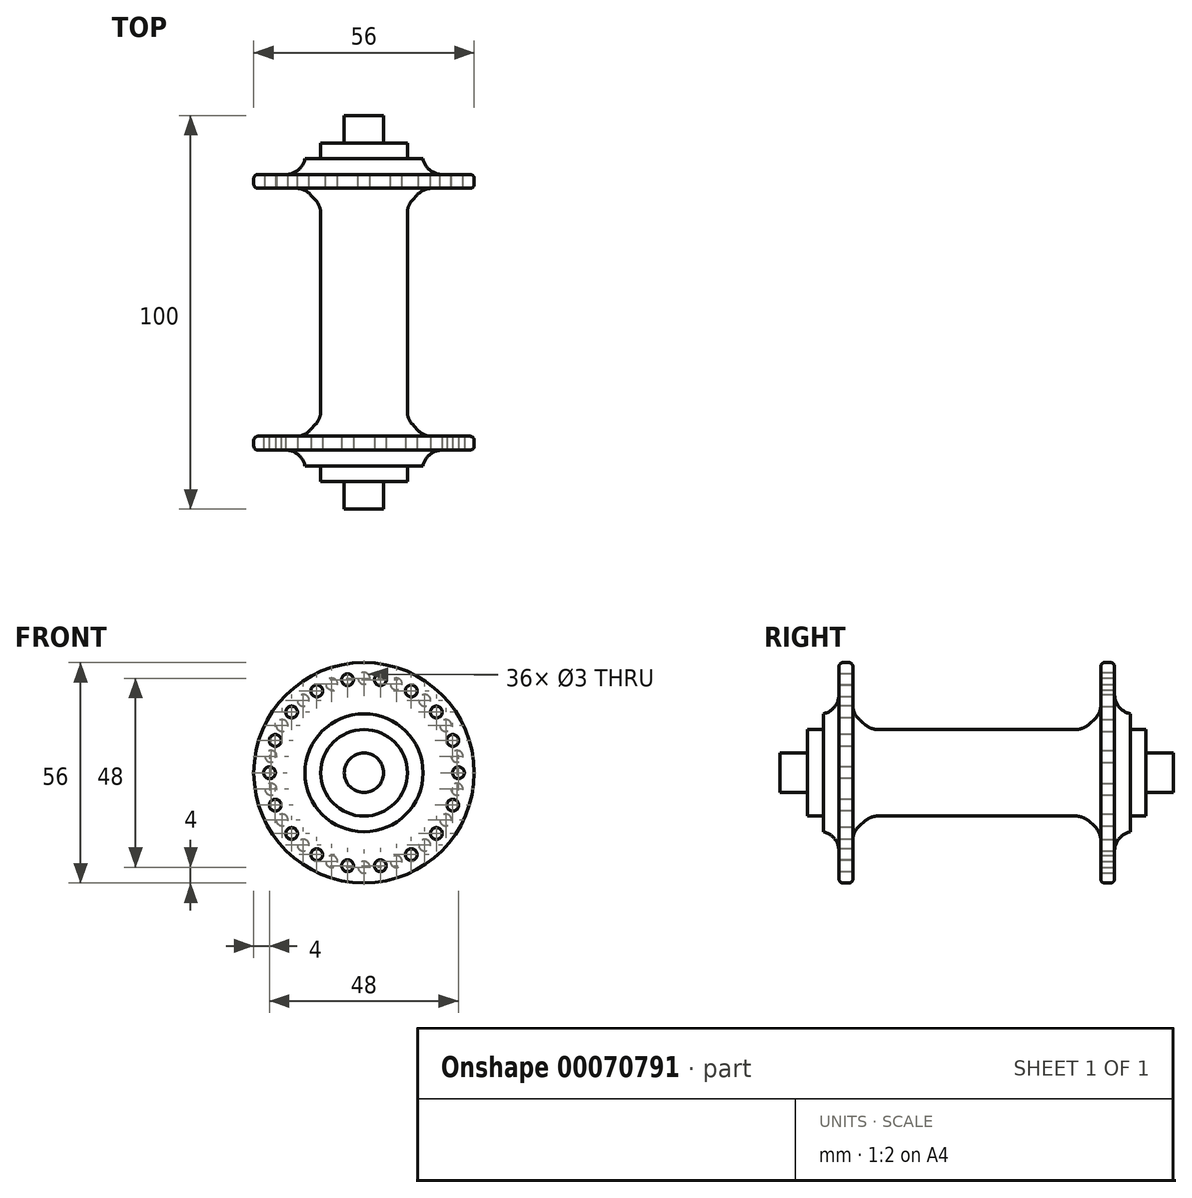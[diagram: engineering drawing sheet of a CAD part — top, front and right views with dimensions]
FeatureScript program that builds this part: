
annotation { "Feature Type Name" : "Feature", "Feature Type Description" : "" }
export const myFeature = defineFeature(function(context is Context, id is Id, definition is map)
    precondition{}
    {
        {
            var Q0;
            Q0=qCreatedBy(makeId("Top.planeOp"),FACE);
            var sketch = newSketch(context, id + "F0", { "sketchPlane" : qUnion([Q0])});
            skLineSegment(sketch, "E0", {"start": v(0, 0) * mm, "end": v(0, 50) * mm});
            skLineSegment(sketch, "E1", {"start": v(0, 50) * mm, "end": v(5, 50) * mm});
            skLineSegment(sketch, "E2", {"start": v(5, 50) * mm, "end": v(5, 43) * mm});
            skLineSegment(sketch, "E3", {"start": v(5, 43) * mm, "end": v(11, 43) * mm});
            skLineSegment(sketch, "E4", {"start": v(11, 43) * mm, "end": v(11, 39) * mm});
            skLineSegment(sketch, "E5", {"start": v(11, 39) * mm, "end": v(15, 39) * mm});
            skLineSegment(sketch, "E6", {"start": v(15, 39) * mm, "end": v(15, 35) * mm});
            skLineSegment(sketch, "E7", {"start": v(15, 35) * mm, "end": v(28, 35) * mm});
            skLineSegment(sketch, "E8", {"start": v(28, 35) * mm, "end": v(28, 31.5) * mm});
            skLineSegment(sketch, "E9", {"start": v(28, 31.5) * mm, "end": v(15, 31.5) * mm});
            skLineSegment(sketch, "E10", {"start": v(15, 31.5) * mm, "end": v(11, 27.03) * mm});
            skLineSegment(sketch, "E11", {"start": v(11, 27.03) * mm, "end": v(11, 0) * mm});
            skLineSegment(sketch, "E12", {"start": v(11, 0) * mm, "end": v(0, 0) * mm});
            skSolve(sketch);
        }
        {
            var Q0;
            Q0=makeQuery(id+"F0.imprint","IMPRINT",FACE,{"disambiguationData":[TD([[makeQuery(id+"F0.imprint","IMPRINT",EDGE,{"derivedFrom":sQuery(id+"F0.wireOp",EDGE,"E0")}),-1.0]])]});
            var Q1;
            Q1=sQuery(id+"F0.wireOp",EDGE,"E0");
            revolve(context, id + "F1", {"entities" : qUnion([Q0]), "axis" : qUnion([Q1]), "revolveType" : RevolveType.FULL});
        }
        {
            var Q0;
            Q0=makeQuery(id+"F1.opRevolve","SWEPT_EDGE",EDGE,{"disambiguationData":[OSD([sQuery(id+"F0.wireOp",EDGE,"E8"),sQuery(id+"F0.wireOp",EDGE,"E9")])]});
            var Q1;
            Q1=makeQuery(id+"F1.opRevolve","SWEPT_EDGE",EDGE,{"disambiguationData":[OSD([sQuery(id+"F0.wireOp",EDGE,"E7"),sQuery(id+"F0.wireOp",EDGE,"E8")])]});
            fillet(context, id + "F2", {"entities" : qUnion([Q0, Q1]), "radius" : 1 * mm, "tangentPropagation" : true, "allowEdgeOverflow" : false});
        }
        {
            var Q0;
            Q0=makeQuery(id+"F1.opRevolve","SWEPT_EDGE",EDGE,{"disambiguationData":[OSD([sQuery(id+"F0.wireOp",EDGE,"E6"),sQuery(id+"F0.wireOp",EDGE,"E7")])]});
            var Q1;
            Q1=makeQuery(id+"F1.opRevolve","SWEPT_EDGE",EDGE,{"disambiguationData":[OSD([sQuery(id+"F0.wireOp",EDGE,"E9"),sQuery(id+"F0.wireOp",EDGE,"E10")])]});
            var Q2;
            Q2=makeQuery(id+"F1.opRevolve","SWEPT_EDGE",EDGE,{"disambiguationData":[OSD([sQuery(id+"F0.wireOp",EDGE,"E10"),sQuery(id+"F0.wireOp",EDGE,"E11")])]});
            fillet(context, id + "F3", {"entities" : qUnion([Q0, Q1, Q2]), "radius" : 5 * mm, "tangentPropagation" : true, "allowEdgeOverflow" : false});
        }
        {
            var Q0;
            Q0=makeQuery(id+"F1.opRevolve","SWEPT_BODY",BODY,{"disambiguationData":[OSD([sQuery(id+"F0.wireOp",EDGE,"E0"),sQuery(id+"F0.wireOp",EDGE,"E1"),sQuery(id+"F0.wireOp",EDGE,"E2"),sQuery(id+"F0.wireOp",EDGE,"E3"),sQuery(id+"F0.wireOp",EDGE,"E4"),sQuery(id+"F0.wireOp",EDGE,"E5"),sQuery(id+"F0.wireOp",EDGE,"E6"),sQuery(id+"F0.wireOp",EDGE,"E7"),sQuery(id+"F0.wireOp",EDGE,"E8"),sQuery(id+"F0.wireOp",EDGE,"E9"),sQuery(id+"F0.wireOp",EDGE,"E10"),sQuery(id+"F0.wireOp",EDGE,"E11"),sQuery(id+"F0.wireOp",EDGE,"E12")])]});
            var Q1;
            Q1=qCreatedBy(makeId("Front.planeOp"),FACE);
            mirror(context, id + "F4", {"operationType" : NewBodyOperationType.ADD, "entities" : qUnion([Q0]), "mirrorPlane" : qUnion([Q1])});
        }
        {
            var Q0;
            Q0=makeQuery(id+"F1.opRevolve","SWEPT_FACE",FACE,{"disambiguationData":[OSD([sQuery(id+"F0.wireOp",EDGE,"E7")])]});
            var sketch = newSketch(context, id + "F5", { "sketchPlane" : qUnion([Q0])});
            skCircle(sketch, "E13", {"center": v(0, 24) * mm, "radius": 1.5 * mm});
            skCircle(sketch, "E14.1.0", {"center": v(-8.2, 22.55) * mm, "radius": 1.5 * mm});
            skCircle(sketch, "E14.2.0", {"center": v(-15.43, 18.39) * mm, "radius": 1.5 * mm});
            skCircle(sketch, "E14.3.0", {"center": v(-20.78, 12) * mm, "radius": 1.5 * mm});
            skCircle(sketch, "E14.4.0", {"center": v(-23.64, 4.17) * mm, "radius": 1.5 * mm});
            skCircle(sketch, "E14.5.0", {"center": v(-23.64, -4.17) * mm, "radius": 1.5 * mm});
            skCircle(sketch, "E14.6.0", {"center": v(-20.78, -12) * mm, "radius": 1.5 * mm});
            skCircle(sketch, "E14.7.0", {"center": v(-15.43, -18.39) * mm, "radius": 1.5 * mm});
            skCircle(sketch, "E14.8.0", {"center": v(-8.2, -22.55) * mm, "radius": 1.5 * mm});
            skCircle(sketch, "E14.9.0", {"center": v(0, -24) * mm, "radius": 1.5 * mm});
            skCircle(sketch, "E14.10.0", {"center": v(8.2, -22.55) * mm, "radius": 1.5 * mm});
            skCircle(sketch, "E14.11.0", {"center": v(15.43, -18.39) * mm, "radius": 1.5 * mm});
            skCircle(sketch, "E14.12.0", {"center": v(20.78, -12) * mm, "radius": 1.5 * mm});
            skCircle(sketch, "E14.13.0", {"center": v(23.64, -4.17) * mm, "radius": 1.5 * mm});
            skCircle(sketch, "E14.14.0", {"center": v(23.64, 4.17) * mm, "radius": 1.5 * mm});
            skCircle(sketch, "E14.15.0", {"center": v(20.78, 12) * mm, "radius": 1.5 * mm});
            skCircle(sketch, "E14.16.0", {"center": v(15.43, 18.39) * mm, "radius": 1.5 * mm});
            skCircle(sketch, "E14.17.0", {"center": v(8.2, 22.55) * mm, "radius": 1.5 * mm});
            skPoint(sketch, "E14.center", {"position": v(0, 0) * mm});
            skSolve(sketch);
        }
        {
            var Q0;
            Q0 = qSketchRegion(id + "F5", true);
            extrude(context, id + "F6", {"entities" : qUnion([Q0]), "operationType" : NewBodyOperationType.REMOVE, "oppositeDirection" : true, "depth" : 25 * mm});
        }
        {
            var Q0;
            Q0=makeQuery(id+"F4.opPattern","COPY",FACE,{"derivedFrom":makeQuery(id+"F1.opRevolve","SWEPT_FACE",FACE,{"disambiguationData":[OSD([sQuery(id+"F0.wireOp",EDGE,"E7")])]}),"instanceName":"1"});
            var sketch = newSketch(context, id + "F7", { "sketchPlane" : qUnion([Q0])});
            skCircle(sketch, "E15", {"center": v(4.17, 23.64) * mm, "radius": 1.5 * mm});
            skLineSegment(sketch, "E16", {"start": v(4.17, 23.64) * mm, "end": v(0, 0) * mm, "construction": true});
            skCircle(sketch, "E17.1.0", {"center": v(-4.17, 23.64) * mm, "radius": 1.5 * mm});
            skCircle(sketch, "E17.2.0", {"center": v(-12, 20.78) * mm, "radius": 1.5 * mm});
            skCircle(sketch, "E17.3.0", {"center": v(-18.39, 15.43) * mm, "radius": 1.5 * mm});
            skCircle(sketch, "E17.4.0", {"center": v(-22.55, 8.2) * mm, "radius": 1.5 * mm});
            skCircle(sketch, "E17.5.0", {"center": v(-24, 0) * mm, "radius": 1.5 * mm});
            skCircle(sketch, "E17.6.0", {"center": v(-22.55, -8.2) * mm, "radius": 1.5 * mm});
            skCircle(sketch, "E17.7.0", {"center": v(-18.39, -15.43) * mm, "radius": 1.5 * mm});
            skCircle(sketch, "E17.8.0", {"center": v(-12, -20.78) * mm, "radius": 1.5 * mm});
            skCircle(sketch, "E17.9.0", {"center": v(-4.17, -23.64) * mm, "radius": 1.5 * mm});
            skCircle(sketch, "E17.10.0", {"center": v(4.17, -23.64) * mm, "radius": 1.5 * mm});
            skCircle(sketch, "E17.11.0", {"center": v(12, -20.78) * mm, "radius": 1.5 * mm});
            skCircle(sketch, "E17.12.0", {"center": v(18.39, -15.43) * mm, "radius": 1.5 * mm});
            skCircle(sketch, "E17.13.0", {"center": v(22.55, -8.2) * mm, "radius": 1.5 * mm});
            skCircle(sketch, "E17.14.0", {"center": v(24, 0) * mm, "radius": 1.5 * mm});
            skCircle(sketch, "E17.15.0", {"center": v(22.55, 8.2) * mm, "radius": 1.5 * mm});
            skCircle(sketch, "E17.16.0", {"center": v(18.39, 15.43) * mm, "radius": 1.5 * mm});
            skCircle(sketch, "E17.17.0", {"center": v(12, 20.78) * mm, "radius": 1.5 * mm});
            skPoint(sketch, "E17.center", {"position": v(0, 0) * mm});
            skSolve(sketch);
        }
        {
            var Q0;
            Q0 = qSketchRegion(id + "F7", true);
            extrude(context, id + "F8", {"entities" : qUnion([Q0]), "operationType" : NewBodyOperationType.REMOVE, "oppositeDirection" : true, "depth" : 25 * mm});
        }
    });
